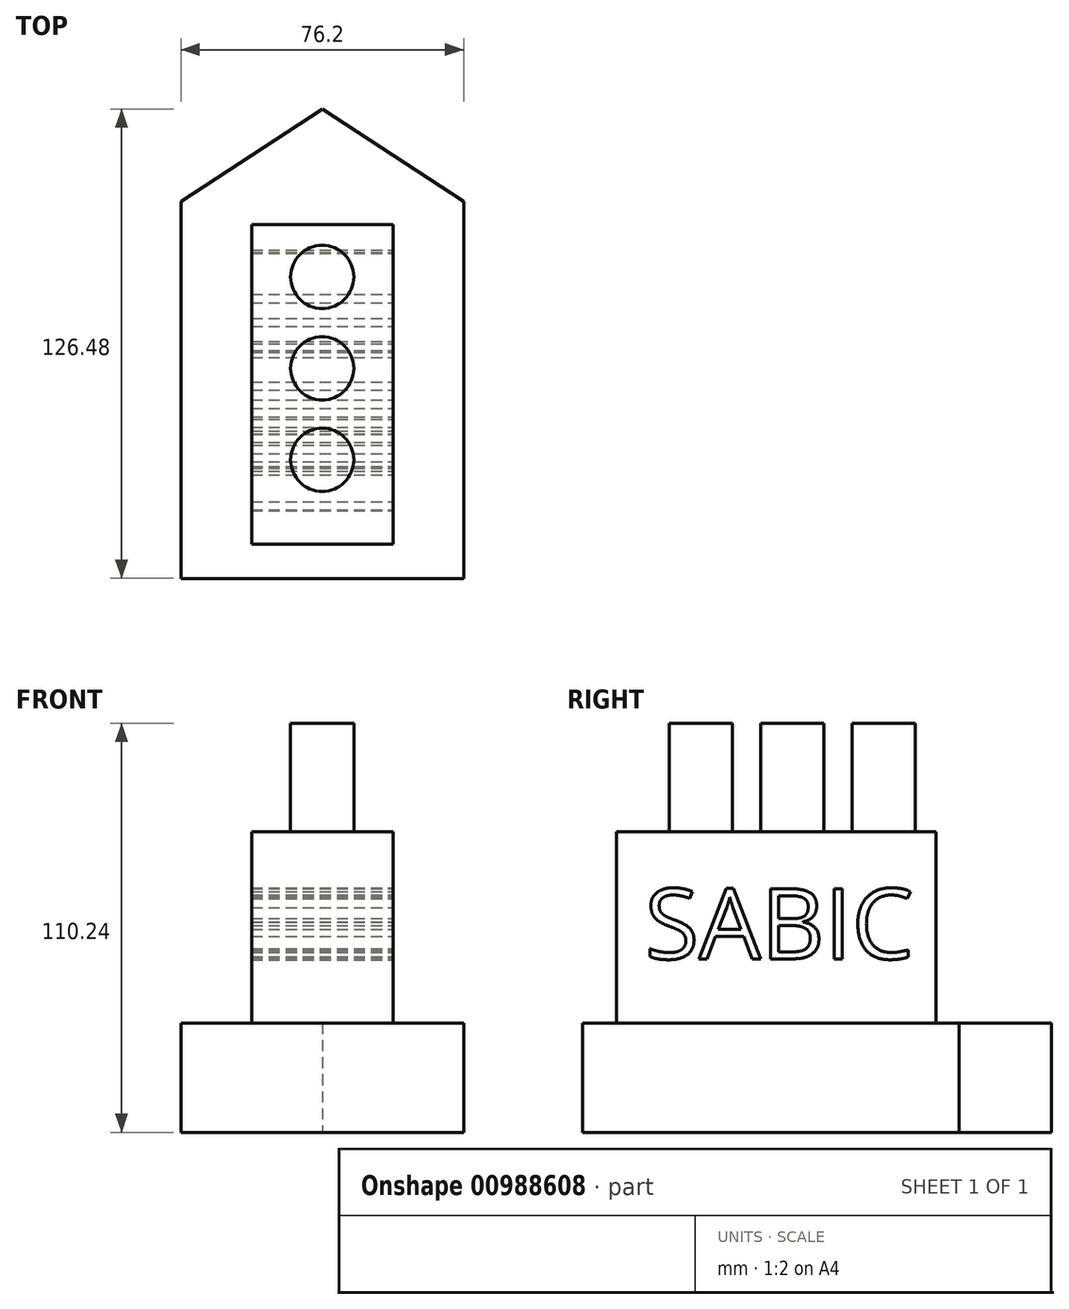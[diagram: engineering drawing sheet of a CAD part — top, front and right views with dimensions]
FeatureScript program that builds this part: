
annotation { "Feature Type Name" : "Feature", "Feature Type Description" : "" }
export const myFeature = defineFeature(function(context is Context, id is Id, definition is map)
    precondition{}
    {
        {
            var Q0;
            Q0=qCreatedBy(makeId("Top.planeOp"),FACE);
            var sketch = newSketch(context, id + "F0", { "sketchPlane" : qUnion([Q0])});
            skLineSegment(sketch, "E0", {"start": v(-38.1, -56.58) * mm, "end": v(38.1, -56.58) * mm});
            skLineSegment(sketch, "E1", {"start": v(38.1, -56.58) * mm, "end": v(38.1, 45.01) * mm});
            skLineSegment(sketch, "E2", {"start": v(38.1, 45.01) * mm, "end": v(0, 69.9) * mm});
            skLineSegment(sketch, "E3", {"start": v(0, 69.9) * mm, "end": v(-38.1, 45.01) * mm});
            skLineSegment(sketch, "E4", {"start": v(-38.1, 45.01) * mm, "end": v(-38.1, -56.58) * mm});
            skSolve(sketch);
        }
        {
            var Q0;
            Q0 = qSketchRegion(id + "F0", true);
            extrude(context, id + "F1", {"entities" : qUnion([Q0]), "depth" : 29.46 * mm, "offsetDistance" : 25.4 * mm});
        }
        {
            var Q0;
            Q0=qCreatedBy(makeId("Top.planeOp"),FACE);
            var sketch = newSketch(context, id + "F2", { "sketchPlane" : qUnion([Q0])});
            skLineSegment(sketch, "E5.bottom", {"start": v(19.05, 38.7) * mm, "end": v(-19.05, 38.7) * mm});
            skLineSegment(sketch, "E5.top", {"start": v(19.05, -47.34) * mm, "end": v(-19.05, -47.34) * mm});
            skLineSegment(sketch, "E5.left", {"start": v(19.05, 38.7) * mm, "end": v(19.05, -47.34) * mm});
            skLineSegment(sketch, "E5.right", {"start": v(-19.05, 38.7) * mm, "end": v(-19.05, -47.34) * mm});
            skSolve(sketch);
        }
        {
            var Q0;
            Q0 = qSketchRegion(id + "F2", true);
            extrude(context, id + "F3", {"entities" : qUnion([Q0]), "operationType" : NewBodyOperationType.ADD, "depth" : 81.03 * mm, "offsetDistance" : 25.4 * mm});
        }
        {
            var Q0;
            Q0=qCreatedBy(makeId("Top.planeOp"),FACE);
            var sketch = newSketch(context, id + "F4", { "sketchPlane" : qUnion([Q0])});
            skCircle(sketch, "E6", {"center": v(0, 24.64) * mm, "radius": 8.5 * mm});
            skCircle(sketch, "E7", {"center": v(0, 0) * mm, "radius": 8.5 * mm});
            skCircle(sketch, "E8", {"center": v(0, -24.64) * mm, "radius": 8.5 * mm});
            skSolve(sketch);
        }
        {
            var Q0;
            Q0 = qSketchRegion(id + "F4", true);
            extrude(context, id + "F5", {"entities" : qUnion([Q0]), "operationType" : NewBodyOperationType.ADD, "depth" : 110.24 * mm, "offsetDistance" : 25.4 * mm});
        }
        {
            var Q0;
            Q0=makeQuery(id+"F3.opExtrude","SWEPT_FACE",FACE,{"disambiguationData":[OSD([sQuery(id+"F2.wireOp",EDGE,"E5.left")])]});
            var sketch = newSketch(context, id + "F6", { "sketchPlane" : qUnion([Q0])});
            skText(sketch, "E9", { "text": "SABIC", "fontName": "OpenSans-Regular.ttf"});
            const initialGuessF6  = {"E9": [-0.03972, 0.04675, 1, 0, 0.01904]};
            skSetInitialGuess(sketch, initialGuessF6);
            skSolve(sketch);
        }
        {
            var Q0;
            Q0 = qSketchRegion(id + "F6", true);
            extrude(context, id + "F7", {"entities" : qUnion([Q0]), "operationType" : NewBodyOperationType.REMOVE, "oppositeDirection" : true, "depth" : 42.42 * mm, "offsetDistance" : 25.4 * mm});
        }
    });
